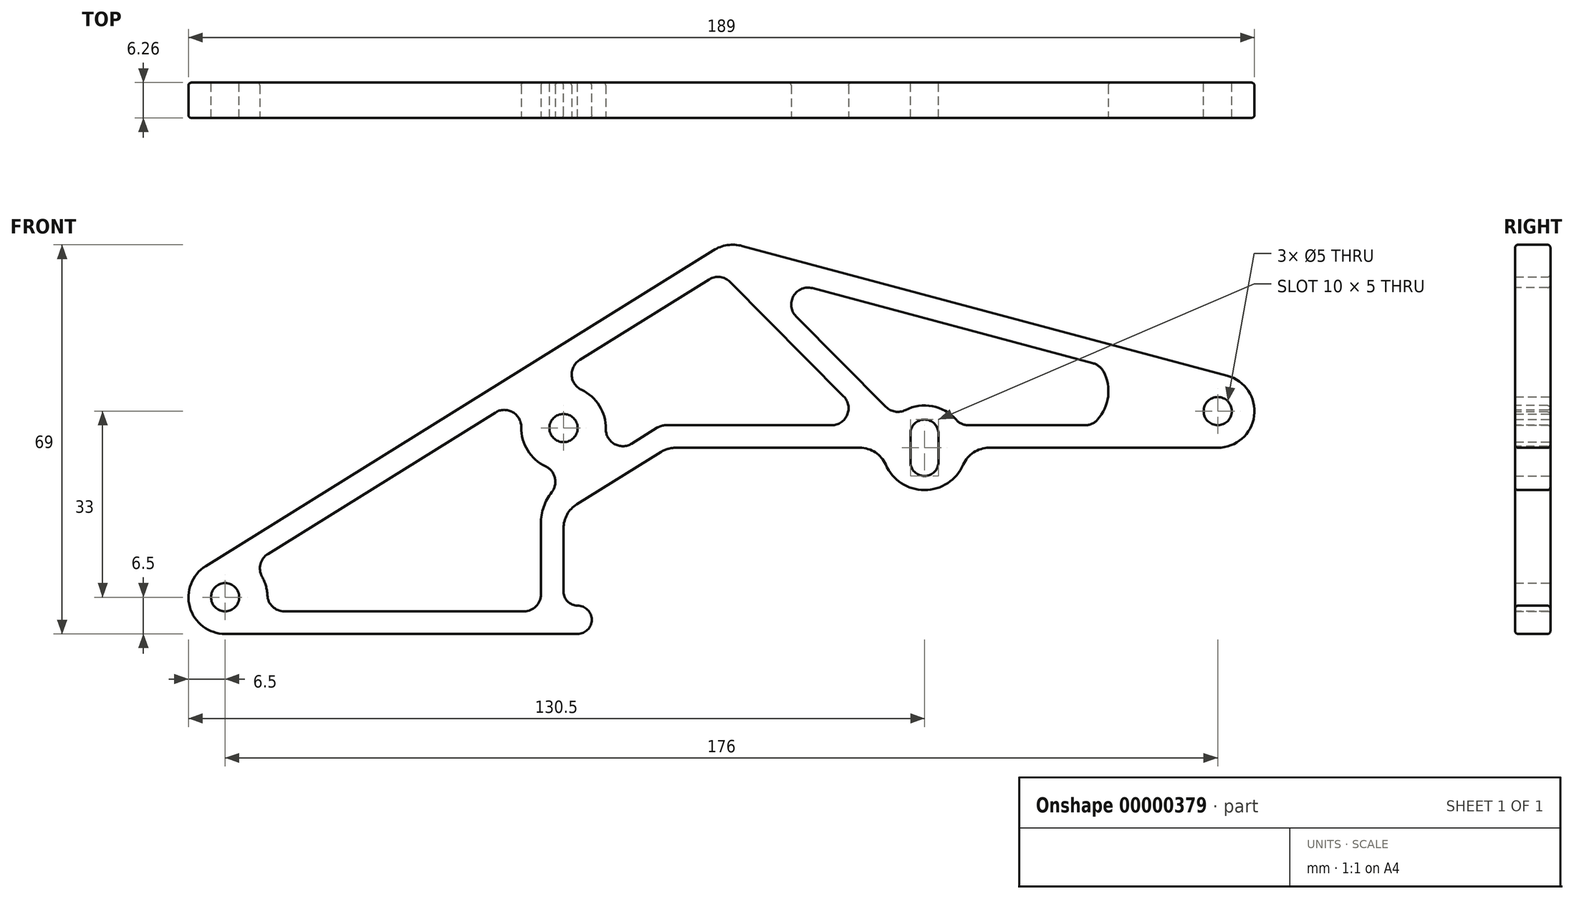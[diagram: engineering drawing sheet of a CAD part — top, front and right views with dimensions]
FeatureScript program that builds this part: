
annotation { "Feature Type Name" : "Feature", "Feature Type Description" : "" }
export const myFeature = defineFeature(function(context is Context, id is Id, definition is map)
    precondition{}
    {
        {
            var Q0;
            Q0=qCreatedBy(makeId("Front.planeOp"),FACE);
            var sketch = newSketch(context, id + "F0", { "sketchPlane" : qUnion([Q0])});
            skCircle(sketch, "E0", {"center": v(0, 0) * mm, "radius": 2.5 * mm});
            skCircle(sketch, "E1", {"center": v(60, 30) * mm, "radius": 2.5 * mm});
            skLineSegment(sketch, "E2", {"start": v(124, 29) * mm, "end": v(124, 24) * mm, "construction": true});
            skCircle(sketch, "E3", {"center": v(124, 29) * mm, "radius": 2.5 * mm});
            skCircle(sketch, "E4", {"center": v(124, 24) * mm, "radius": 2.5 * mm});
            skLineSegment(sketch, "E5", {"start": v(121.5, 29) * mm, "end": v(121.5, 24) * mm});
            skLineSegment(sketch, "E6", {"start": v(126.5, 29) * mm, "end": v(126.5, 24) * mm});
            skCircle(sketch, "E7", {"center": v(149.11, 36.5) * mm, "radius": 2.5 * mm});
            skCircle(sketch, "E8", {"center": v(176, 33) * mm, "radius": 2.5 * mm});
            skPoint(sketch, "E9", {"position": v(124, 26.5) * mm});
            skPoint(sketch, "E10", {"position": v(90, 62.5) * mm});
            skCircle(sketch, "E11", {"center": v(0, 0) * mm, "radius": 6.5 * mm});
            skCircle(sketch, "E12", {"center": v(149.11, 36.5) * mm, "radius": 10 * mm, "construction": true});
            skCircle(sketch, "E13", {"center": v(176, 33) * mm, "radius": 6.5 * mm, "construction": true});
            skLineSegment(sketch, "E14", {"start": v(90, 62.5) * mm, "end": v(177.66, 39.28) * mm, "construction": true});
            skLineSegment(sketch, "E15", {"start": v(176, 26.5) * mm, "end": v(135.57, 26.5) * mm, "construction": true});
            skSolve(sketch);
        }
        {
            var Q0;
            Q0=qCreatedBy(makeId("Front.planeOp"),FACE);
            var sketch = newSketch(context, id + "F1", { "sketchPlane" : qUnion([Q0])});
            skCircle(sketch, "E16.0", {"center": v(0, 0) * mm, "radius": 6.5 * mm});
            skCircle(sketch, "E17", {"center": v(176, 33) * mm, "radius": 6.5 * mm});
            skCircle(sketch, "E18", {"center": v(90, 56) * mm, "radius": 6.5 * mm});
            skLineSegment(sketch, "E19", {"start": v(-3.43, 5.52) * mm, "end": v(86.57, 61.52) * mm});
            skLineSegment(sketch, "E20", {"start": v(91.68, 62.28) * mm, "end": v(177.68, 39.28) * mm});
            skCircle(sketch, "E21", {"center": v(124, 26.5) * mm, "radius": 7.5 * mm});
            skLineSegment(sketch, "E22", {"start": v(176, 26.5) * mm, "end": v(176, 26.5) * mm});
            skLineSegment(sketch, "E23", {"start": v(176, 26.5) * mm, "end": v(78.46, 26.5) * mm});
            skLineSegment(sketch, "E24", {"start": v(60, 15.01) * mm, "end": v(60, -6.5) * mm});
            skLineSegment(sketch, "E25", {"start": v(0, -6.5) * mm, "end": v(62.5, -6.5) * mm});
            skCircle(sketch, "E26", {"center": v(62.5, -4) * mm, "radius": 2.5 * mm});
            skLineSegment(sketch, "E27", {"start": v(62.5, -1.5) * mm, "end": v(60, -1.5) * mm});
            skLineSegment(sketch, "E28", {"start": v(60, 15.01) * mm, "end": v(78.46, 26.5) * mm});
            skLineSegment(sketch, "E29", {"start": v(60, 30) * mm, "end": v(53.28, 40.8) * mm, "construction": true});
            skLineSegment(sketch, "E30", {"start": v(60, 30) * mm, "end": v(66.72, 19.2) * mm, "construction": true});
            skSolve(sketch);
        }
        {
            var Q0;
            {var subQ0=sQuery(id+"F1.wireOp",EDGE,"E23");var subQ1=sQuery(id+"F1.wireOp",EDGE,"E21");var subQ3=makeQuery(id+"F1.imprint","INTERSECT",VERTEX,{"disambiguationData":[OD(0.0)],"derivedFrom":[subQ1,subQ0]});Q0=makeQuery(id+"F1.imprint","IMPRINT",FACE,{"disambiguationData":[TD([[makeQuery(id+"F1.imprint","IMPRINT",EDGE,{"disambiguationData":[TD([[subQ3,1.0]])],"derivedFrom":subQ1}),1.0]])]});}
            var Q1;
            {var subQ0=sQuery(id+"F1.wireOp",EDGE,"E27");Q1=makeQuery(id+"F1.imprint","IMPRINT",FACE,{"disambiguationData":[TD([[makeQuery(id+"F1.imprint","IMPRINT",EDGE,{"derivedFrom":subQ0}),1.0]])]});}
            var Q2;
            {var subQ1=sQuery(id+"F1.wireOp",EDGE,"E24");var subQ3=sQuery(id+"F1.wireOp",EDGE,"E25");var subQ5=makeQuery(id+"F1.imprint","INTERSECT",VERTEX,{"derivedFrom":[subQ1,subQ3]});Q2=makeQuery(id+"F1.imprint","IMPRINT",FACE,{"disambiguationData":[TD([[makeQuery(id+"F1.imprint","IMPRINT",EDGE,{"disambiguationData":[TD([[subQ5,1.0]])],"derivedFrom":subQ1}),1.0]])]});}
            var Q3;
            {var subQ0=sQuery(id+"F1.wireOp",EDGE,"E16.0");var subQ2=makeQuery(id+"F1.imprint","INTERSECT",VERTEX,{"derivedFrom":[subQ0,sQuery(id+"F1.wireOp",EDGE,"E19")]});Q3=makeQuery(id+"F1.imprint","IMPRINT",FACE,{"disambiguationData":[TD([[makeQuery(id+"F1.imprint","IMPRINT",EDGE,{"disambiguationData":[TD([[subQ2,-1.0]])],"derivedFrom":subQ0}),1.0]])]});}
            var Q4;
            {var subQ0=sQuery(id+"F1.wireOp",EDGE,"E17");var subQ2=makeQuery(id+"F1.imprint","INTERSECT",VERTEX,{"derivedFrom":[subQ0,sQuery(id+"F1.wireOp",EDGE,"E20")]});Q4=makeQuery(id+"F1.imprint","IMPRINT",FACE,{"disambiguationData":[TD([[makeQuery(id+"F1.imprint","IMPRINT",EDGE,{"disambiguationData":[TD([[subQ2,-1.0]])],"derivedFrom":subQ0}),1.0]])]});}
            var Q5;
            {var subQ0=sQuery(id+"F1.wireOp",EDGE,"E26");var subQ1=makeQuery(id+"F1.imprint","INTERSECT",VERTEX,{"derivedFrom":[subQ0,sQuery(id+"F1.wireOp",EDGE,"E27")]});Q5=makeQuery(id+"F1.imprint","IMPRINT",FACE,{"disambiguationData":[TD([[makeQuery(id+"F1.imprint","IMPRINT",EDGE,{"disambiguationData":[TD([[subQ1,-1.0]])],"derivedFrom":subQ0}),1.0]])]});}
            var Q6;
            {var subQ0=sQuery(id+"F1.wireOp",EDGE,"E18");var subQ2=makeQuery(id+"F1.imprint","INTERSECT",VERTEX,{"derivedFrom":[subQ0,sQuery(id+"F1.wireOp",EDGE,"E19")]});Q6=makeQuery(id+"F1.imprint","IMPRINT",FACE,{"disambiguationData":[TD([[makeQuery(id+"F1.imprint","IMPRINT",EDGE,{"disambiguationData":[TD([[subQ2,1.0]])],"derivedFrom":subQ0}),1.0]])]});}
            var Q7;
            {var subQ0=sQuery(id+"F1.wireOp",EDGE,"E23");var subQ1=sQuery(id+"F1.wireOp",EDGE,"E21");var subQ3=makeQuery(id+"F1.imprint","INTERSECT",VERTEX,{"disambiguationData":[OD(0.0)],"derivedFrom":[subQ1,subQ0]});Q7=makeQuery(id+"F1.imprint","IMPRINT",FACE,{"disambiguationData":[TD([[makeQuery(id+"F1.imprint","IMPRINT",EDGE,{"disambiguationData":[TD([[subQ3,-1.0]])],"derivedFrom":subQ1}),1.0]])]});}
            var Q8;
            {var subQ15=sQuery(id+"F1.wireOp",EDGE,"E19");Q8=makeQuery(id+"F1.imprint","IMPRINT",FACE,{"disambiguationData":[TD([[makeQuery(id+"F1.imprint","IMPRINT",EDGE,{"derivedFrom":subQ15}),-1.0]])]});}
            extrude(context, id + "F2", {"entities" : qUnion([Q0, Q1, Q2, Q3, Q4, Q5, Q6, Q7, Q8]), "endBound" : BoundingType.SYMMETRIC, "depth" : 6.25 * mm});
        }
        {
            var Q0;
            Q0=makeQuery(id+"F0.imprint","IMPRINT",FACE,{"disambiguationData":[TD([[makeQuery(id+"F0.imprint","IMPRINT",EDGE,{"derivedFrom":sQuery(id+"F0.wireOp",EDGE,"E1")}),1.0]])]});
            var Q1;
            Q1=makeQuery(id+"F0.imprint","IMPRINT",FACE,{"disambiguationData":[TD([[makeQuery(id+"F0.imprint","IMPRINT",EDGE,{"derivedFrom":sQuery(id+"F0.wireOp",EDGE,"E7")}),1.0]])]});
            var Q2;
            Q2=makeQuery(id+"F0.imprint","IMPRINT",FACE,{"disambiguationData":[TD([[makeQuery(id+"F0.imprint","IMPRINT",EDGE,{"derivedFrom":sQuery(id+"F0.wireOp",EDGE,"E8")}),1.0]])]});
            var Q3;
            {var subQ0=sQuery(id+"F0.wireOp",EDGE,"E5");Q3=makeQuery(id+"F0.imprint","IMPRINT",FACE,{"disambiguationData":[TD([[makeQuery(id+"F0.imprint","IMPRINT",EDGE,{"derivedFrom":subQ0}),1.0]])]});}
            var Q4;
            {var subQ0=sQuery(id+"F0.wireOp",EDGE,"E3");var subQ3=makeQuery(id+"F0.imprint","INTERSECT",VERTEX,{"derivedFrom":[subQ0,sQuery(id+"F0.wireOp",EDGE,"E5")]});Q4=makeQuery(id+"F0.imprint","IMPRINT",FACE,{"disambiguationData":[TD([[makeQuery(id+"F0.imprint","IMPRINT",EDGE,{"disambiguationData":[TD([[subQ3,1.0]])],"derivedFrom":subQ0}),1.0]])]});}
            var Q5;
            {var subQ0=sQuery(id+"F0.wireOp",EDGE,"E4");var subQ1=makeQuery(id+"F0.imprint","INTERSECT",VERTEX,{"derivedFrom":[subQ0,sQuery(id+"F0.wireOp",EDGE,"E6")]});Q5=makeQuery(id+"F0.imprint","IMPRINT",FACE,{"disambiguationData":[TD([[makeQuery(id+"F0.imprint","IMPRINT",EDGE,{"disambiguationData":[TD([[subQ1,-1.0]])],"derivedFrom":subQ0}),1.0]])]});}
            var Q6;
            {var subQ0=sQuery(id+"F0.wireOp",EDGE,"E6");Q6=makeQuery(id+"F0.imprint","IMPRINT",FACE,{"disambiguationData":[TD([[makeQuery(id+"F0.imprint","IMPRINT",EDGE,{"derivedFrom":subQ0}),-1.0]])]});}
            var Q7;
            Q7=makeQuery(id+"F0.imprint","IMPRINT",FACE,{"disambiguationData":[TD([[makeQuery(id+"F0.imprint","IMPRINT",EDGE,{"derivedFrom":sQuery(id+"F0.wireOp",EDGE,"E0")}),1.0]])]});
            extrude(context, id + "F3", {"entities" : qUnion([Q0, Q1, Q2, Q3, Q4, Q5, Q6, Q7]), "operationType" : NewBodyOperationType.REMOVE, "endBound" : BoundingType.SYMMETRIC, "depth" : 25 * mm});
        }
        {
            var Q0;
            Q0=makeQuery(id+"F2.opExtrude","SWEPT_EDGE",EDGE,{"disambiguationData":[OSD([sQuery(id+"F1.wireOp",EDGE,"E24"),sQuery(id+"F1.wireOp",EDGE,"E28")])]});
            var Q1;
            Q1=makeQuery(id+"F2.opExtrude","SWEPT_EDGE",EDGE,{"disambiguationData":[OSD([sQuery(id+"F1.wireOp",EDGE,"E23"),sQuery(id+"F1.wireOp",EDGE,"E28")])]});
            var Q2;
            {var subQ0=sQuery(id+"F1.wireOp",EDGE,"E21");var subQ1=sQuery(id+"F1.wireOp",EDGE,"E23");Q2=makeQuery(id+"F2.opExtrude","SWEPT_EDGE",EDGE,{"disambiguationData":[OSD([subQ0,subQ1]),TDD([makeQuery(id+"F1.imprint","INTERSECT",VERTEX,{"disambiguationData":[OD(1.0)],"derivedFrom":[subQ0,subQ1]})])]});}
            var Q3;
            {var subQ0=sQuery(id+"F1.wireOp",EDGE,"E21");var subQ1=sQuery(id+"F1.wireOp",EDGE,"E23");Q3=makeQuery(id+"F2.opExtrude","SWEPT_EDGE",EDGE,{"disambiguationData":[OSD([subQ0,subQ1]),TDD([makeQuery(id+"F1.imprint","INTERSECT",VERTEX,{"disambiguationData":[OD(0.0)],"derivedFrom":[subQ0,subQ1]})])]});}
            fillet(context, id + "F4", {"entities" : qUnion([Q0, Q1, Q2, Q3]), "radius" : 5 * mm, "tangentPropagation" : true, "allowEdgeOverflow" : false});
        }
        {
            var Q0;
            Q0=makeQuery(id+"F2.opExtrude","SWEPT_EDGE",EDGE,{"disambiguationData":[OSD([sQuery(id+"F1.wireOp",EDGE,"E24"),sQuery(id+"F1.wireOp",EDGE,"E27")])]});
            fillet(context, id + "F5", {"entities" : qUnion([Q0]), "radius" : 2.5 * mm, "tangentPropagation" : true, "allowEdgeOverflow" : false});
        }
        {
            var Q0;
            Q0=qCreatedBy(makeId("Front.planeOp"),FACE);
            var sketch = newSketch(context, id + "F6", { "sketchPlane" : qUnion([Q0])});
            skCircle(sketch, "E31", {"center": v(0, 0) * mm, "radius": 7.5 * mm});
            skCircle(sketch, "E32", {"center": v(60, 30) * mm, "radius": 7.5 * mm});
            skCircle(sketch, "E33", {"center": v(149.11, 36.5) * mm, "radius": 7.5 * mm});
            skCircle(sketch, "E34", {"center": v(176, 33) * mm, "radius": 7.5 * mm});
            skSolve(sketch);
        }
        {
            var Q0;
            Q0=makeQuery(id+"F2.opExtrude","CAP_FACE",FACE,{"disambiguationData":[OSD([sQuery(id+"F1.wireOp",EDGE,"E16.0"),sQuery(id+"F1.wireOp",EDGE,"E17"),sQuery(id+"F1.wireOp",EDGE,"E18"),sQuery(id+"F1.wireOp",EDGE,"E19"),sQuery(id+"F1.wireOp",EDGE,"E20"),sQuery(id+"F1.wireOp",EDGE,"E21"),sQuery(id+"F1.wireOp",EDGE,"E23"),sQuery(id+"F1.wireOp",EDGE,"E24"),sQuery(id+"F1.wireOp",EDGE,"E25"),sQuery(id+"F1.wireOp",EDGE,"E26"),sQuery(id+"F1.wireOp",EDGE,"E27"),sQuery(id+"F1.wireOp",EDGE,"E28")])],"isStart":false});
            var sketch = newSketch(context, id + "F7", { "sketchPlane" : qUnion([Q0])});
            skLineSegment(sketch, "E35.0", {"start": v(-8.75, -2.5) * mm, "end": v(89.6, 58.7) * mm});
            skLineSegment(sketch, "E36", {"start": v(65.66, 48.51) * mm, "end": v(67.77, 45.11) * mm, "construction": true});
            skLineSegment(sketch, "E37", {"start": v(-8.75, -2.5) * mm, "end": v(56, -2.5) * mm});
            skLineSegment(sketch, "E38", {"start": v(77.32, 30.5) * mm, "end": v(56, 17.23) * mm});
            skLineSegment(sketch, "E39", {"start": v(77.32, 30.5) * mm, "end": v(176, 30.5) * mm});
            skLineSegment(sketch, "E40", {"start": v(89.6, 58.7) * mm, "end": v(176.65, 35.42) * mm});
            skLineSegment(sketch, "E41", {"start": v(31.23, -2.5) * mm, "end": v(31.23, -6.5) * mm, "construction": true});
            skLineSegment(sketch, "E42", {"start": v(56, 7.87) * mm, "end": v(60, 7.87) * mm, "construction": true});
            skLineSegment(sketch, "E43", {"start": v(66.66, 23.87) * mm, "end": v(68.77, 20.47) * mm});
            skLineSegment(sketch, "E44", {"start": v(101.97, 30.5) * mm, "end": v(101.97, 26.5) * mm, "construction": true});
            skLineSegment(sketch, "E45", {"start": v(142.31, 44.6) * mm, "end": v(143.35, 48.46) * mm});
            skCircle(sketch, "E46", {"center": v(124, 26.5) * mm, "radius": 7.5 * mm});
            skLineSegment(sketch, "E47", {"start": v(89.6, 58.7) * mm, "end": v(124, 24) * mm, "construction": true});
            skLineSegment(sketch, "E48", {"start": v(93.43, 57.67) * mm, "end": v(118.9, 32) * mm});
            skLineSegment(sketch, "E49.0.MirrorCS", {"start": v(87.86, 57.61) * mm, "end": v(116.76, 28.46) * mm});
            skLineSegment(sketch, "E50", {"start": v(106.83, 44.16) * mm, "end": v(103.99, 41.34) * mm, "construction": true});
            skPoint(sketch, "E51", {"position": v(105.4, 42.75) * mm});
            skCircle(sketch, "E52", {"center": v(49.5, 30.21) * mm, "radius": 3 * mm});
            skCircle(sketch, "E53", {"center": v(55.55, 20.49) * mm, "radius": 3 * mm});
            skCircle(sketch, "E54", {"center": v(64.45, 39.51) * mm, "radius": 3 * mm});
            skCircle(sketch, "E55", {"center": v(70.5, 29.79) * mm, "radius": 3 * mm});
            skLineSegment(sketch, "E56", {"start": v(56, -2.5) * mm, "end": v(56, 17.23) * mm});
            skCircle(sketch, "E57.0", {"center": v(0, 0) * mm, "radius": 7.5 * mm});
            skCircle(sketch, "E57.1", {"center": v(60, 30) * mm, "radius": 7.5 * mm});
            skCircle(sketch, "E58.0", {"center": v(149.11, 36.5) * mm, "radius": 7.5 * mm});
            skCircle(sketch, "E58.1", {"center": v(176, 33) * mm, "radius": 7.5 * mm});
            skCircle(sketch, "E59.0", {"center": v(176, 33) * mm, "radius": 2.5 * mm});
            skPoint(sketch, "E60.orphan", {"position": v(195.02, 30.5) * mm});
            skSolve(sketch);
        }
        {
            var Q0;
            Q0=makeQuery(id+"F7.imprint","IMPRINT",FACE,{"disambiguationData":[TD([[sQuery(id+"F7.imprint",EDGE,"39a8ea26-989f-4e51-98c3-9f7a15ca03cc"),-1.0]])]});
            var Q1;
            {var subQ5=sQuery(id+"F7.wireOp",EDGE,"E49.0.MirrorCS");var subQ8=sQuery(id+"F7.wireOp",EDGE,"E35.0");var subQ9=makeQuery(id+"F7.imprint","INTERSECT",VERTEX,{"derivedFrom":[subQ8,subQ5]});Q1=makeQuery(id+"F7.imprint","IMPRINT",FACE,{"disambiguationData":[TD([[makeQuery(id+"F7.imprint","IMPRINT",EDGE,{"disambiguationData":[TD([[subQ9,1.0]])],"derivedFrom":subQ8}),-1.0]])]});}
            var Q2;
            {var subQ0=sQuery(id+"F7.wireOp",EDGE,"E48");Q2=makeQuery(id+"F7.imprint","IMPRINT",FACE,{"disambiguationData":[TD([[makeQuery(id+"F7.imprint","IMPRINT",EDGE,{"derivedFrom":subQ0}),1.0]])]});}
            var Q3;
            {var subQ3=sQuery(id+"F7.wireOp",EDGE,"E39");var subQ5=sQuery(id+"F7.wireOp",EDGE,"E58.0");var subQ7=makeQuery(id+"F7.imprint","INTERSECT",VERTEX,{"disambiguationData":[OD(1.0)],"derivedFrom":[subQ3,subQ5]});Q3=makeQuery(id+"F7.imprint","IMPRINT",FACE,{"disambiguationData":[TD([[makeQuery(id+"F7.imprint","IMPRINT",EDGE,{"disambiguationData":[TD([[subQ7,-1.0]])],"derivedFrom":subQ3}),1.0]])]});}
            var Q4;
            {var subQ10=sQuery(id+"F7.wireOp",EDGE,"E56");Q4=makeQuery(id+"F7.imprint","IMPRINT",FACE,{"disambiguationData":[TD([[makeQuery(id+"F7.imprint","IMPRINT",EDGE,{"derivedFrom":subQ10}),1.0]])]});}
            var Q5;
            {var subQ0=sQuery(id+"F7.wireOp",EDGE,"E52");var subQ2=makeQuery(id+"F7.imprint","INTERSECT",VERTEX,{"derivedFrom":[sQuery(id+"F7.wireOp",EDGE,"E35.0"),subQ0]});Q5=makeQuery(id+"F7.imprint","IMPRINT",FACE,{"disambiguationData":[TD([[makeQuery(id+"F7.imprint","IMPRINT",EDGE,{"disambiguationData":[TD([[subQ2,-1.0]])],"derivedFrom":subQ0}),1.0]])]});}
            var Q6;
            {var subQ0=sQuery(id+"F7.wireOp",EDGE,"E53");var subQ2=makeQuery(id+"F7.imprint","INTERSECT",VERTEX,{"derivedFrom":[sQuery(id+"F7.wireOp",EDGE,"E38"),subQ0]});Q6=makeQuery(id+"F7.imprint","IMPRINT",FACE,{"disambiguationData":[TD([[makeQuery(id+"F7.imprint","IMPRINT",EDGE,{"disambiguationData":[TD([[subQ2,1.0]])],"derivedFrom":subQ0}),1.0]])]});}
            var Q7;
            {var subQ0=sQuery(id+"F7.wireOp",EDGE,"E55");var subQ2=makeQuery(id+"F7.imprint","INTERSECT",VERTEX,{"derivedFrom":[sQuery(id+"F7.wireOp",EDGE,"E38"),subQ0]});Q7=makeQuery(id+"F7.imprint","IMPRINT",FACE,{"disambiguationData":[TD([[makeQuery(id+"F7.imprint","IMPRINT",EDGE,{"disambiguationData":[TD([[subQ2,1.0]])],"derivedFrom":subQ0}),1.0]])]});}
            var Q8;
            {var subQ0=sQuery(id+"F7.wireOp",EDGE,"E54");var subQ2=makeQuery(id+"F7.imprint","INTERSECT",VERTEX,{"derivedFrom":[sQuery(id+"F7.wireOp",EDGE,"E35.0"),subQ0]});Q8=makeQuery(id+"F7.imprint","IMPRINT",FACE,{"disambiguationData":[TD([[makeQuery(id+"F7.imprint","IMPRINT",EDGE,{"disambiguationData":[TD([[subQ2,-1.0]])],"derivedFrom":subQ0}),1.0]])]});}
            extrude(context, id + "F8", {"entities" : qUnion([Q0, Q1, Q2, Q3, Q4, Q5, Q6, Q7, Q8]), "operationType" : NewBodyOperationType.REMOVE, "endBound" : BoundingType.THROUGH_ALL, "oppositeDirection" : true, "depth" : 25 * mm});
        }
        {
            var Q0;
            {var subQ0=sQuery(id+"F7.wireOp",EDGE,"E38");Q0=qUnion([makeQuery(id+"F8.boolean.opBoolean","COPY",EDGE,{"derivedFrom":makeQuery(id+"F8.opExtrude","SWEPT_EDGE",EDGE,{"disambiguationData":[OSD([subQ0,sQuery(id+"F7.wireOp",EDGE,"E55")])]})}),makeQuery(id+"F8.boolean.opBoolean","COPY",EDGE,{"derivedFrom":makeQuery(id+"F8.opExtrude","SWEPT_EDGE",EDGE,{"disambiguationData":[OSD([subQ0,sQuery(id+"F7.wireOp",EDGE,"E53")])]})})]);}
            var Q1;
            {var subQ0=sQuery(id+"F7.wireOp",EDGE,"E35.0");Q1=qUnion([makeQuery(id+"F8.boolean.opBoolean","COPY",EDGE,{"derivedFrom":makeQuery(id+"F8.opExtrude","SWEPT_EDGE",EDGE,{"disambiguationData":[OSD([subQ0,sQuery(id+"F7.wireOp",EDGE,"E57.0")])]})}),makeQuery(id+"F8.boolean.opBoolean","COPY",EDGE,{"derivedFrom":makeQuery(id+"F8.opExtrude","SWEPT_EDGE",EDGE,{"disambiguationData":[OSD([subQ0,sQuery(id+"F7.wireOp",EDGE,"E54")])]})}),makeQuery(id+"F8.boolean.opBoolean","COPY",EDGE,{"derivedFrom":makeQuery(id+"F8.opExtrude","SWEPT_EDGE",EDGE,{"disambiguationData":[OSD([subQ0,sQuery(id+"F7.wireOp",EDGE,"E52")])]})})]);}
            var Q2;
            {var subQ0=sQuery(id+"F7.wireOp",EDGE,"E35.0");Q2=qUnion([makeQuery(id+"F8.boolean.opBoolean","COPY",EDGE,{"derivedFrom":makeQuery(id+"F8.opExtrude","SWEPT_EDGE",EDGE,{"disambiguationData":[OSD([subQ0,sQuery(id+"F7.wireOp",EDGE,"E57.0")])]})}),makeQuery(id+"F8.boolean.opBoolean","COPY",EDGE,{"derivedFrom":makeQuery(id+"F8.opExtrude","SWEPT_EDGE",EDGE,{"disambiguationData":[OSD([subQ0,sQuery(id+"F7.wireOp",EDGE,"E54")])]})}),makeQuery(id+"F8.boolean.opBoolean","COPY",EDGE,{"derivedFrom":makeQuery(id+"F8.opExtrude","SWEPT_EDGE",EDGE,{"disambiguationData":[OSD([subQ0,sQuery(id+"F7.wireOp",EDGE,"E52")])]})})]);}
            var Q3;
            Q3=makeQuery(id+"F8.boolean.opBoolean","COPY",EDGE,{"derivedFrom":makeQuery(id+"F8.opExtrude","SWEPT_EDGE",EDGE,{"disambiguationData":[OSD([sQuery(id+"F7.wireOp",EDGE,"E37"),sQuery(id+"F7.wireOp",EDGE,"E57.0")])]})});
            var Q4;
            Q4=makeQuery(id+"F8.boolean.opBoolean","COPY",EDGE,{"derivedFrom":makeQuery(id+"F8.opExtrude","SWEPT_EDGE",EDGE,{"disambiguationData":[OSD([sQuery(id+"F7.wireOp",EDGE,"E37"),sQuery(id+"F7.wireOp",EDGE,"E56")])]})});
            var Q5;
            {var subQ0=sQuery(id+"F7.wireOp",EDGE,"E38");Q5=qUnion([makeQuery(id+"F8.boolean.opBoolean","COPY",EDGE,{"derivedFrom":makeQuery(id+"F8.opExtrude","SWEPT_EDGE",EDGE,{"disambiguationData":[OSD([subQ0,sQuery(id+"F7.wireOp",EDGE,"E55")])]})}),makeQuery(id+"F8.boolean.opBoolean","COPY",EDGE,{"derivedFrom":makeQuery(id+"F8.opExtrude","SWEPT_EDGE",EDGE,{"disambiguationData":[OSD([subQ0,sQuery(id+"F7.wireOp",EDGE,"E53")])]})})]);}
            var Q6;
            {var subQ0=sQuery(id+"F7.wireOp",EDGE,"E35.0");Q6=qUnion([makeQuery(id+"F8.boolean.opBoolean","COPY",EDGE,{"derivedFrom":makeQuery(id+"F8.opExtrude","SWEPT_EDGE",EDGE,{"disambiguationData":[OSD([subQ0,sQuery(id+"F7.wireOp",EDGE,"E57.0")])]})}),makeQuery(id+"F8.boolean.opBoolean","COPY",EDGE,{"derivedFrom":makeQuery(id+"F8.opExtrude","SWEPT_EDGE",EDGE,{"disambiguationData":[OSD([subQ0,sQuery(id+"F7.wireOp",EDGE,"E54")])]})}),makeQuery(id+"F8.boolean.opBoolean","COPY",EDGE,{"derivedFrom":makeQuery(id+"F8.opExtrude","SWEPT_EDGE",EDGE,{"disambiguationData":[OSD([subQ0,sQuery(id+"F7.wireOp",EDGE,"E52")])]})})]);}
            var Q7;
            Q7=makeQuery(id+"F8.boolean.opBoolean","COPY",EDGE,{"derivedFrom":makeQuery(id+"F8.opExtrude","SWEPT_EDGE",EDGE,{"disambiguationData":[OSD([sQuery(id+"F7.wireOp",EDGE,"E35.0"),sQuery(id+"F7.wireOp",EDGE,"E49.0.MirrorCS")])]})});
            var Q8;
            Q8=makeQuery(id+"F8.boolean.opBoolean","COPY",EDGE,{"derivedFrom":makeQuery(id+"F8.opExtrude","SWEPT_EDGE",EDGE,{"disambiguationData":[OSD([sQuery(id+"F7.imprint",VERTEX,"E49.0.MirrorCS.end")])]})});
            var Q9;
            Q9=makeQuery(id+"F8.boolean.opBoolean","COPY",EDGE,{"derivedFrom":makeQuery(id+"F8.opExtrude","SWEPT_EDGE",EDGE,{"disambiguationData":[OSD([sQuery(id+"F7.wireOp",EDGE,"E46"),sQuery(id+"F7.wireOp",EDGE,"E48")])]})});
            var Q10;
            Q10=makeQuery(id+"F8.boolean.opBoolean","COPY",EDGE,{"derivedFrom":makeQuery(id+"F8.opExtrude","SWEPT_EDGE",EDGE,{"disambiguationData":[OSD([sQuery(id+"F7.wireOp",EDGE,"E40"),sQuery(id+"F7.wireOp",EDGE,"E48")])]})});
            var Q11;
            {var subQ0=sQuery(id+"F7.wireOp",EDGE,"E40");var subQ1=sQuery(id+"F7.wireOp",EDGE,"E58.0");Q11=makeQuery(id+"F8.boolean.opBoolean","COPY",EDGE,{"derivedFrom":makeQuery(id+"F8.opExtrude","SWEPT_EDGE",EDGE,{"disambiguationData":[OSD([subQ0,subQ1]),TDD([makeQuery(id+"F7.imprint","INTERSECT",VERTEX,{"disambiguationData":[OD(0.0)],"derivedFrom":[subQ0,subQ1]})])]})});}
            var Q12;
            {var subQ0=sQuery(id+"F7.wireOp",EDGE,"E39");var subQ1=sQuery(id+"F7.wireOp",EDGE,"E58.0");Q12=makeQuery(id+"F8.boolean.opBoolean","COPY",EDGE,{"derivedFrom":makeQuery(id+"F8.opExtrude","SWEPT_EDGE",EDGE,{"disambiguationData":[OSD([subQ0,subQ1]),TDD([makeQuery(id+"F7.imprint","INTERSECT",VERTEX,{"disambiguationData":[OD(0.0)],"derivedFrom":[subQ0,subQ1]})])]})});}
            var Q13;
            {var subQ0=sQuery(id+"F7.wireOp",EDGE,"E39");var subQ1=sQuery(id+"F7.wireOp",EDGE,"E58.0");Q13=makeQuery(id+"F8.boolean.opBoolean","COPY",EDGE,{"derivedFrom":makeQuery(id+"F8.opExtrude","SWEPT_EDGE",EDGE,{"disambiguationData":[OSD([subQ0,subQ1]),TDD([makeQuery(id+"F7.imprint","INTERSECT",VERTEX,{"disambiguationData":[OD(1.0)],"derivedFrom":[subQ0,subQ1]})])]})});}
            var Q14;
            {var subQ0=sQuery(id+"F7.wireOp",EDGE,"E40");var subQ1=sQuery(id+"F7.wireOp",EDGE,"E58.0");Q14=makeQuery(id+"F8.boolean.opBoolean","COPY",EDGE,{"derivedFrom":makeQuery(id+"F8.opExtrude","SWEPT_EDGE",EDGE,{"disambiguationData":[OSD([subQ0,subQ1]),TDD([makeQuery(id+"F7.imprint","INTERSECT",VERTEX,{"disambiguationData":[OD(1.0)],"derivedFrom":[subQ0,subQ1]})])]})});}
            var Q15;
            {var subQ0=sQuery(id+"F7.wireOp",EDGE,"E40");var subQ1=sQuery(id+"F7.wireOp",EDGE,"E58.0");Q15=qUnion([makeQuery(id+"F8.boolean.opBoolean","COPY",EDGE,{"derivedFrom":makeQuery(id+"F8.opExtrude","SWEPT_EDGE",EDGE,{"disambiguationData":[OSD([subQ0,sQuery(id+"F7.wireOp",EDGE,"E58.1")])]})}),makeQuery(id+"F8.boolean.opBoolean","COPY",EDGE,{"derivedFrom":makeQuery(id+"F8.opExtrude","SWEPT_EDGE",EDGE,{"disambiguationData":[OSD([subQ0,subQ1]),TDD([makeQuery(id+"F7.imprint","INTERSECT",VERTEX,{"disambiguationData":[OD(0.0)],"derivedFrom":[subQ0,subQ1]})])]})}),makeQuery(id+"F8.boolean.opBoolean","COPY",EDGE,{"derivedFrom":makeQuery(id+"F8.opExtrude","SWEPT_EDGE",EDGE,{"disambiguationData":[OSD([subQ0,subQ1]),TDD([makeQuery(id+"F7.imprint","INTERSECT",VERTEX,{"disambiguationData":[OD(1.0)],"derivedFrom":[subQ0,subQ1]})])]})})]);}
            var Q16;
            {var subQ0=sQuery(id+"F7.wireOp",EDGE,"E39");var subQ1=sQuery(id+"F7.wireOp",EDGE,"E58.0");Q16=qUnion([makeQuery(id+"F8.boolean.opBoolean","COPY",EDGE,{"derivedFrom":makeQuery(id+"F8.opExtrude","SWEPT_EDGE",EDGE,{"disambiguationData":[OSD([subQ0,sQuery(id+"F7.wireOp",EDGE,"E46")])]})}),makeQuery(id+"F8.boolean.opBoolean","COPY",EDGE,{"derivedFrom":makeQuery(id+"F8.opExtrude","SWEPT_EDGE",EDGE,{"disambiguationData":[OSD([subQ0,sQuery(id+"F7.wireOp",EDGE,"E58.1")])]})}),makeQuery(id+"F8.boolean.opBoolean","COPY",EDGE,{"derivedFrom":makeQuery(id+"F8.opExtrude","SWEPT_EDGE",EDGE,{"disambiguationData":[OSD([subQ0,subQ1]),TDD([makeQuery(id+"F7.imprint","INTERSECT",VERTEX,{"disambiguationData":[OD(0.0)],"derivedFrom":[subQ0,subQ1]})])]})}),makeQuery(id+"F8.boolean.opBoolean","COPY",EDGE,{"derivedFrom":makeQuery(id+"F8.opExtrude","SWEPT_EDGE",EDGE,{"disambiguationData":[OSD([subQ0,sQuery(id+"F7.wireOp",EDGE,"E49.0.MirrorCS")])]})}),makeQuery(id+"F8.boolean.opBoolean","COPY",EDGE,{"derivedFrom":makeQuery(id+"F8.opExtrude","SWEPT_EDGE",EDGE,{"disambiguationData":[OSD([subQ0,subQ1]),TDD([makeQuery(id+"F7.imprint","INTERSECT",VERTEX,{"disambiguationData":[OD(1.0)],"derivedFrom":[subQ0,subQ1]})])]})})]);}
            var Q17;
            Q17=makeQuery(id+"F8.boolean.opBoolean","COPY",EDGE,{"derivedFrom":makeQuery(id+"F8.opExtrude","SWEPT_EDGE",EDGE,{"disambiguationData":[OSD([sQuery(id+"F7.wireOp",EDGE,"E39"),sQuery(id+"F7.wireOp",EDGE,"E46")])]})});
            var Q18;
            Q18=makeQuery(id+"F8.boolean.opBoolean","COPY",EDGE,{"derivedFrom":makeQuery(id+"F8.opExtrude","SWEPT_EDGE",EDGE,{"disambiguationData":[OSD([sQuery(id+"F7.imprint",VERTEX,"E56.end")])]})});
            fillet(context, id + "F9", {"entities" : qUnion([Q0, Q1, Q2, Q3, Q4, Q5, Q6, Q7, Q8, Q9, Q10, Q11, Q12, Q13, Q14, Q15, Q16, Q17, Q18]), "radius" : 3 * mm, "tangentPropagation" : true, "allowEdgeOverflow" : false});
        }
        {
            var Q0;
            Q0=makeQuery(id+"F8.boolean.opBoolean","COPY",EDGE,{"derivedFrom":makeQuery(id+"F8.opExtrude","SWEPT_EDGE",EDGE,{"disambiguationData":[OSD([sQuery(id+"F7.wireOp",EDGE,"E38"),sQuery(id+"F7.wireOp",EDGE,"E39")])]})});
            var Q1;
            Q1=makeQuery(id+"F8.boolean.opBoolean","COPY",EDGE,{"derivedFrom":makeQuery(id+"F8.opExtrude","SWEPT_EDGE",EDGE,{"disambiguationData":[OSD([sQuery(id+"F7.wireOp",EDGE,"E38"),sQuery(id+"F7.wireOp",EDGE,"E56")])]})});
            fillet(context, id + "F10", {"entities" : qUnion([Q0, Q1]), "radius" : 9 * mm, "tangentPropagation" : true, "allowEdgeOverflow" : false});
        }
        {
            var Q0;
            Q0=makeQuery(id+"F2.opExtrude","CAP_EDGE",EDGE,{"disambiguationData":[OSD([sQuery(id+"F1.wireOp",EDGE,"E19")])],"isStart":false});
            var Q1;
            {var subQ0=sQuery(id+"F7.wireOp",EDGE,"E35.0");Q1=makeQuery(id+"F8.boolean.opBoolean","COPY",EDGE,{"derivedFrom":makeQuery(id+"F8.opExtrude","CAP_EDGE",EDGE,{"disambiguationData":[OSD([subQ0]),TDD([makeQuery(id+"F7.imprint","IMPRINT",EDGE,{"disambiguationData":[TD([[makeQuery(id+"F7.imprint","INTERSECT",VERTEX,{"disambiguationData":[OD(1.0)],"derivedFrom":[subQ0,sQuery(id+"F7.wireOp",EDGE,"E57.0")]}),-1.0]])],"derivedFrom":subQ0})])],"isStart":true})});}
            var Q2;
            {var subQ0=sQuery(id+"F7.wireOp",EDGE,"E35.0");Q2=makeQuery(id+"F8.boolean.opBoolean","COPY",EDGE,{"derivedFrom":makeQuery(id+"F8.opExtrude","CAP_EDGE",EDGE,{"disambiguationData":[OSD([subQ0]),TDD([makeQuery(id+"F7.imprint","IMPRINT",EDGE,{"disambiguationData":[TD([[makeQuery(id+"F7.imprint","INTERSECT",VERTEX,{"derivedFrom":[subQ0,sQuery(id+"F7.wireOp",EDGE,"E49.0.MirrorCS")]}),1.0]])],"derivedFrom":subQ0})])],"isStart":true})});}
            var Q3;
            {var subQ0=sQuery(id+"F7.wireOp",EDGE,"E40");var subQ1=makeQuery(id+"F7.imprint","INTERSECT",VERTEX,{"derivedFrom":[subQ0,sQuery(id+"F7.wireOp",EDGE,"E45")]});Q3=makeQuery(id+"F8.boolean.opBoolean","COPY",EDGE,{"derivedFrom":makeQuery(id+"F8.opExtrude","CAP_EDGE",EDGE,{"disambiguationData":[OSD([subQ0]),TDD([makeQuery(id+"F7.imprint","IMPRINT",EDGE,{"disambiguationData":[TD([[subQ1,1.0]])],"derivedFrom":subQ0}),makeQuery(id+"F7.imprint","IMPRINT",EDGE,{"disambiguationData":[TD([[subQ1,-1.0]])],"derivedFrom":subQ0})])],"isStart":true})});}
            var Q4;
            {var subQ0=sQuery(id+"F7.wireOp",EDGE,"E40");Q4=makeQuery(id+"F8.boolean.opBoolean","COPY",EDGE,{"derivedFrom":makeQuery(id+"F8.opExtrude","CAP_EDGE",EDGE,{"disambiguationData":[OSD([subQ0]),TDD([makeQuery(id+"F7.imprint","IMPRINT",EDGE,{"disambiguationData":[TD([[makeQuery(id+"F7.imprint","INTERSECT",VERTEX,{"disambiguationData":[OD(1.0)],"derivedFrom":[subQ0,sQuery(id+"F7.wireOp",EDGE,"E58.0")]}),-1.0]])],"derivedFrom":subQ0})])],"isStart":true})});}
            var Q5;
            Q5=makeQuery(id+"F8.boolean.opBoolean","INTERSECT",EDGE,{"derivedFrom":[makeQuery(id+"F2.opExtrude","CAP_FACE",FACE,{"disambiguationData":[OSD([sQuery(id+"F1.wireOp",EDGE,"E16.0"),sQuery(id+"F1.wireOp",EDGE,"E17"),sQuery(id+"F1.wireOp",EDGE,"E18"),sQuery(id+"F1.wireOp",EDGE,"E19"),sQuery(id+"F1.wireOp",EDGE,"E20"),sQuery(id+"F1.wireOp",EDGE,"E21"),sQuery(id+"F1.wireOp",EDGE,"E23"),sQuery(id+"F1.wireOp",EDGE,"E24"),sQuery(id+"F1.wireOp",EDGE,"E25"),sQuery(id+"F1.wireOp",EDGE,"E26"),sQuery(id+"F1.wireOp",EDGE,"E27"),sQuery(id+"F1.wireOp",EDGE,"E28")])],"isStart":true}),makeQuery(id+"F8.opExtrude","SWEPT_FACE",FACE,{"disambiguationData":[OSD([sQuery(id+"F7.wireOp",EDGE,"E37")])]})]});
            var Q6;
            {var subQ0=sQuery(id+"F7.wireOp",EDGE,"E39");Q6=makeQuery(id+"F8.boolean.opBoolean","INTERSECT",EDGE,{"derivedFrom":[makeQuery(id+"F2.opExtrude","CAP_FACE",FACE,{"disambiguationData":[OSD([sQuery(id+"F1.wireOp",EDGE,"E16.0"),sQuery(id+"F1.wireOp",EDGE,"E17"),sQuery(id+"F1.wireOp",EDGE,"E18"),sQuery(id+"F1.wireOp",EDGE,"E19"),sQuery(id+"F1.wireOp",EDGE,"E20"),sQuery(id+"F1.wireOp",EDGE,"E21"),sQuery(id+"F1.wireOp",EDGE,"E23"),sQuery(id+"F1.wireOp",EDGE,"E24"),sQuery(id+"F1.wireOp",EDGE,"E25"),sQuery(id+"F1.wireOp",EDGE,"E26"),sQuery(id+"F1.wireOp",EDGE,"E27"),sQuery(id+"F1.wireOp",EDGE,"E28")])],"isStart":true}),makeQuery(id+"F8.opExtrude","SWEPT_FACE",FACE,{"disambiguationData":[OSD([subQ0]),TDD([makeQuery(id+"F7.imprint","IMPRINT",EDGE,{"disambiguationData":[TD([[makeQuery(id+"F7.imprint","INTERSECT",VERTEX,{"derivedFrom":[sQuery(id+"F7.wireOp",EDGE,"E38"),subQ0]}),-1.0]])],"derivedFrom":subQ0})])]})]});}
            var Q7;
            {var subQ0=sQuery(id+"F7.wireOp",EDGE,"E39");Q7=makeQuery(id+"F8.boolean.opBoolean","INTERSECT",EDGE,{"derivedFrom":[makeQuery(id+"F2.opExtrude","CAP_FACE",FACE,{"disambiguationData":[OSD([sQuery(id+"F1.wireOp",EDGE,"E16.0"),sQuery(id+"F1.wireOp",EDGE,"E17"),sQuery(id+"F1.wireOp",EDGE,"E18"),sQuery(id+"F1.wireOp",EDGE,"E19"),sQuery(id+"F1.wireOp",EDGE,"E20"),sQuery(id+"F1.wireOp",EDGE,"E21"),sQuery(id+"F1.wireOp",EDGE,"E23"),sQuery(id+"F1.wireOp",EDGE,"E24"),sQuery(id+"F1.wireOp",EDGE,"E25"),sQuery(id+"F1.wireOp",EDGE,"E26"),sQuery(id+"F1.wireOp",EDGE,"E27"),sQuery(id+"F1.wireOp",EDGE,"E28")])],"isStart":true}),makeQuery(id+"F8.opExtrude","SWEPT_FACE",FACE,{"disambiguationData":[OSD([subQ0]),TDD([makeQuery(id+"F7.imprint","IMPRINT",EDGE,{"disambiguationData":[TD([[makeQuery(id+"F7.imprint","INTERSECT",VERTEX,{"disambiguationData":[OD(1.0)],"derivedFrom":[subQ0,sQuery(id+"F7.wireOp",EDGE,"E46")]}),-1.0]])],"derivedFrom":subQ0})])]})]});}
            var Q8;
            {var subQ0=sQuery(id+"F7.wireOp",EDGE,"E40");Q8=makeQuery(id+"F8.boolean.opBoolean","INTERSECT",EDGE,{"derivedFrom":[makeQuery(id+"F2.opExtrude","CAP_FACE",FACE,{"disambiguationData":[OSD([sQuery(id+"F1.wireOp",EDGE,"E16.0"),sQuery(id+"F1.wireOp",EDGE,"E17"),sQuery(id+"F1.wireOp",EDGE,"E18"),sQuery(id+"F1.wireOp",EDGE,"E19"),sQuery(id+"F1.wireOp",EDGE,"E20"),sQuery(id+"F1.wireOp",EDGE,"E21"),sQuery(id+"F1.wireOp",EDGE,"E23"),sQuery(id+"F1.wireOp",EDGE,"E24"),sQuery(id+"F1.wireOp",EDGE,"E25"),sQuery(id+"F1.wireOp",EDGE,"E26"),sQuery(id+"F1.wireOp",EDGE,"E27"),sQuery(id+"F1.wireOp",EDGE,"E28")])],"isStart":true}),makeQuery(id+"F8.opExtrude","SWEPT_FACE",FACE,{"disambiguationData":[OSD([subQ0]),TDD([makeQuery(id+"F7.imprint","IMPRINT",EDGE,{"disambiguationData":[TD([[makeQuery(id+"F7.imprint","INTERSECT",VERTEX,{"disambiguationData":[OD(1.0)],"derivedFrom":[subQ0,sQuery(id+"F7.wireOp",EDGE,"E58.0")]}),-1.0]])],"derivedFrom":subQ0})])]})]});}
            var Q9;
            Q9=makeQuery(id+"F2.opExtrude","CAP_EDGE",EDGE,{"disambiguationData":[OSD([sQuery(id+"F1.wireOp",EDGE,"E20")])],"isStart":true});
            fillet(context, id + "F11", {"entities" : qUnion([Q0, Q1, Q2, Q3, Q4, Q5, Q6, Q7, Q8, Q9]), "radius" : 0.5 * mm, "tangentPropagation" : true, "allowEdgeOverflow" : false});
        }
    });
